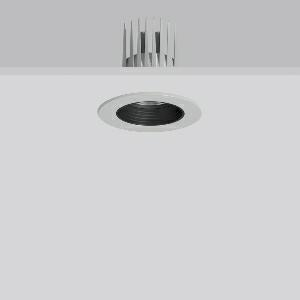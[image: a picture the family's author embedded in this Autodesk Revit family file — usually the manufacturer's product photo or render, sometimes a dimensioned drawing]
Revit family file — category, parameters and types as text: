
# Revit family: heledon_mini_e_901745_004_f9f8
name_source: partatom
category: Lighting Fixtures
units: mm (PartAtom-declared; Revit-internal decimal feet)

## family parameters
Cut with Voids When Loaded = No
Host = Face
Light Source = No
Part Type = Normal
Room Calculation Point = No
Round Connector Dimension = Use Diameter
Shared = No

## types (1)
- HELEDON mini E (1 x LED Modul 930, 2000 lm, 3000)
    Apparent Load = 20 VA
    Approval mark = CE
    CIE Flux Codes = 98 100 100 100 100
    Color Rendering = 90
    Color Temperature = 3000
    Default Elevation = 1800 mm
    Description = Series: HELEDON mini
Round recessed downlight. Housing: die-cast aluminium, powder-coated. Black plastic ring and recessed LED to prevent glare from the side. Optical assembly with lens made of plastic (polycarbonate) for the best homogeneous light distribution - can be changed without tools. Best colour rendering index Ra>90. Suitable for Recessed ceiling mounting. Installation without tools thanks to spring fastening system. Including separate LED converter with connecting cable 600 mm.High quality converter without flickering and stroboscopic effect. Through-wiring box (5 pole) available as accessory. The following accessories can be mounted without use of tools: interchangeable lenses, decorative glasses, honeycomb louvre, clear and frosted diffusers, white interchangeable plastic ring. 
Colour: silver
Diameter: 124 mm
Height: 3 mm
Cut-out diameter: 114 mm
Recess height: 170 mm
Luminaire: recess height: 120 mm
Lamp: LED
Socket: without socket
Colour temperature: 3000K
Colour rendering index (CRI): 92
System power: 20 W
Rated luminous flux: 2000 lm
Luminous efficiency: 100 lm/W
Control gear: Regulated power supply
Protection class: II
Type of protection: IP 20
    Height = 0 mm  [stored 0 ft]
    Lamp = 1 x LED Modul 930
    Lamp Light Flux = 2000 lm
    Lamp count = 1
    Length = 124 mm  [stored 0.406824 ft]
    Lifetime = 50000 h
    Luminous efficacy = 100 lm/W
    Manufacturer = RZB
    ModVariant = No
    Model = 901745.004
    Mounting Place = Ceiling
    Mounting Type = Recessed
    Number of Poles = 1
    OnlyDefault = Yes
    Power Factor = 1
    Product Name = HELEDON mini E
    Product group = Recessed downlights
    ProductGroupID = 402
    Protection Class = Protection class II
    Protection Degree = IP 20
    RLX_Detail_Level = 1
    RLX_Emergency_Light_Flux = 0 lm
    RLX_Emergency_Type = 0
    RLX_Emergency_Type_DB = No
    RlxData = <blob elided: 124289 chars, md5=40d82f96>
    Socket = socket
    Standby Power = 0 W
    System Light Flux = 2000 lm
    System Power = 20 W
    Type Comments = Product without accessories
    Type Image = 901656.004.jpg
    URL = http://relux.com
    VarID = ---
    Voltage = 230 V
    Voltage Range = 220-240 V
    Weight = 0.00 kg
    Width = 0 mm  [stored 0 ft]

note: [stored X ft] marks values corroborated as IEEE doubles in the binary element streams (Revit-internal decimal feet)

## geometry (parser evidence)
native form markers: Blend x4, Sweep x12
no freeform markers — native parametric forms only
